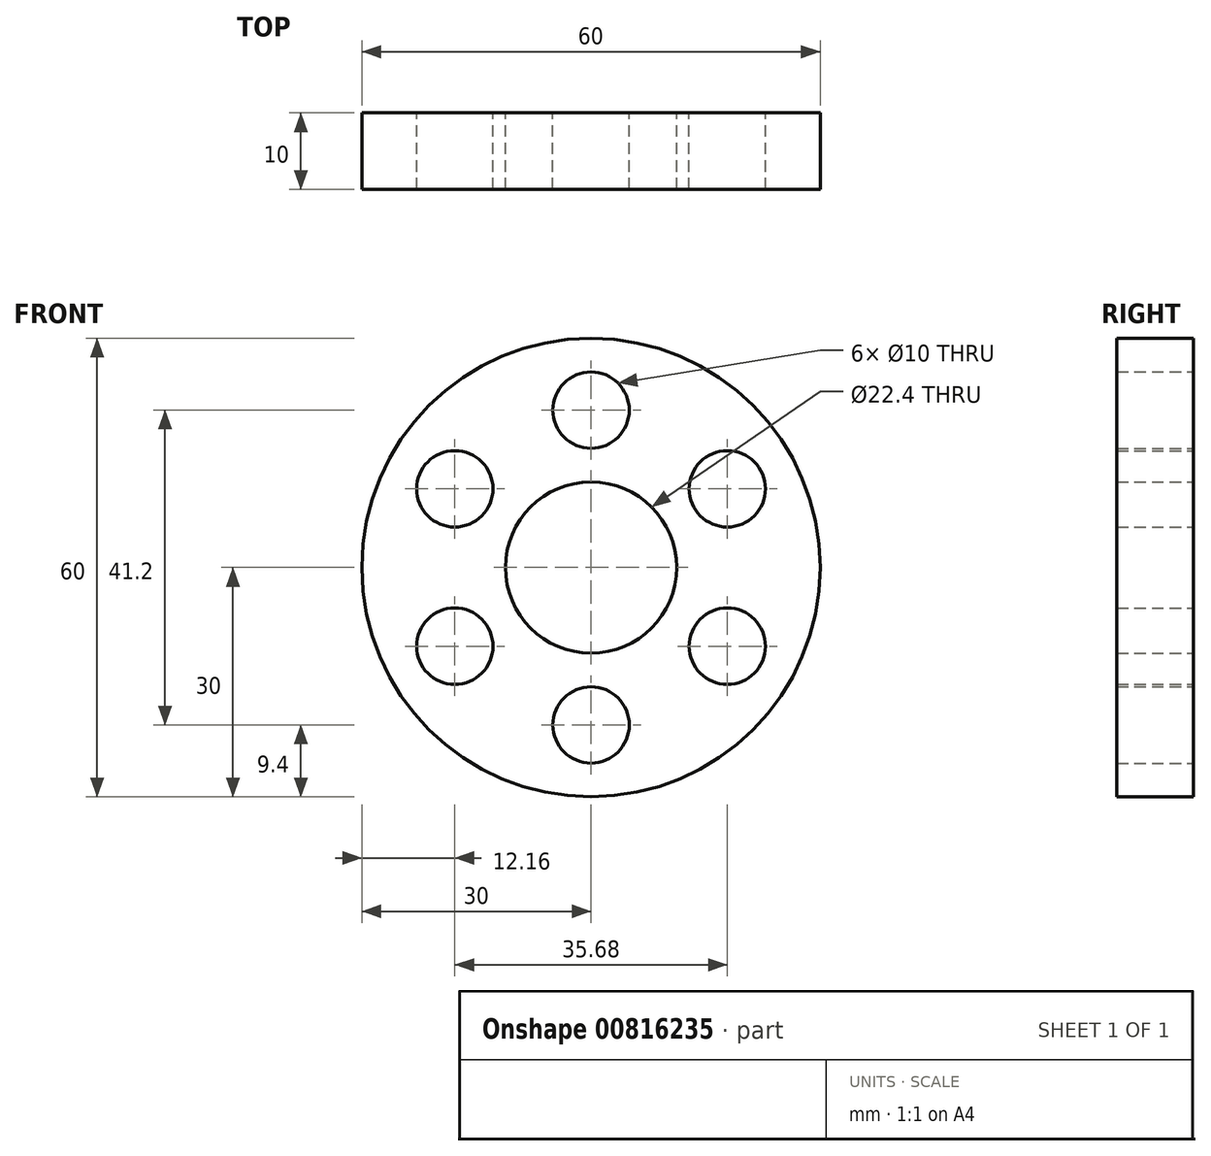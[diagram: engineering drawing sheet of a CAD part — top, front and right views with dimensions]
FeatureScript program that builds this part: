
annotation { "Feature Type Name" : "Feature", "Feature Type Description" : "" }
export const myFeature = defineFeature(function(context is Context, id is Id, definition is map)
    precondition{}
    {
        {
            var Q0;
            Q0=qCreatedBy(makeId("Front.planeOp"),FACE);
            var sketch = newSketch(context, id + "F0", { "sketchPlane" : qUnion([Q0])});
            skCircle(sketch, "E0", {"center": v(0, 0) * mm, "radius": 11.2 * mm});
            skPoint(sketch, "E1.0.midPoint", {"position": v(22.5, 0) * mm});
            skPoint(sketch, "E2.visualSharp", {"position": v(22.5, 38.97) * mm});
            skPoint(sketch, "E3.visualSharp", {"position": v(22.5, -38.97) * mm});
            skPoint(sketch, "E4.visualSharp", {"position": v(-45, 0) * mm});
            skPoint(sketch, "E5.visualSharp", {"position": v(0, 35) * mm});
            skPoint(sketch, "E6.visualSharp", {"position": v(-30.31, -17.5) * mm});
            skPoint(sketch, "E7.visualSharp", {"position": v(30.31, -17.5) * mm});
            skLineSegment(sketch, "E8", {"start": v(0, 35) * mm, "end": v(0, 40) * mm});
            skPoint(sketch, "E9.orphan", {"position": v(0, 11.2) * mm});
            skCircle(sketch, "E10", {"center": v(0, 0) * mm, "radius": 30 * mm});
            skCircle(sketch, "E11", {"center": v(0, 20.6) * mm, "radius": 5 * mm});
            skPoint(sketch, "E12.orphan", {"position": v(0, 30) * mm});
            skCircle(sketch, "E13.1.0", {"center": v(-17.84, 10.3) * mm, "radius": 5 * mm});
            skCircle(sketch, "E13.2.0", {"center": v(-17.84, -10.3) * mm, "radius": 5 * mm});
            skCircle(sketch, "E13.3.0", {"center": v(0, -20.6) * mm, "radius": 5 * mm});
            skCircle(sketch, "E13.4.0", {"center": v(17.84, -10.3) * mm, "radius": 5 * mm});
            skCircle(sketch, "E13.5.0", {"center": v(17.84, 10.3) * mm, "radius": 5 * mm});
            skLineSegment(sketch, "E14", {"start": v(0, -20.6) * mm, "end": v(0, -11.2) * mm});
            skSolve(sketch);
        }
        {
            var Q0;
            Q0 = qSketchRegion(id + "F0", true);
            extrude(context, id + "F1", {"entities" : qUnion([Q0]), "depth" : 7 * mm, "offsetDistance" : 25 * mm});
        }
        {
            var Q0;
            Q0 = qSketchRegion(id + "F0", true);
            extrude(context, id + "F2", {"entities" : qUnion([Q0]), "operationType" : NewBodyOperationType.ADD, "depth" : 10 * mm, "offsetDistance" : 25 * mm});
        }
    });
